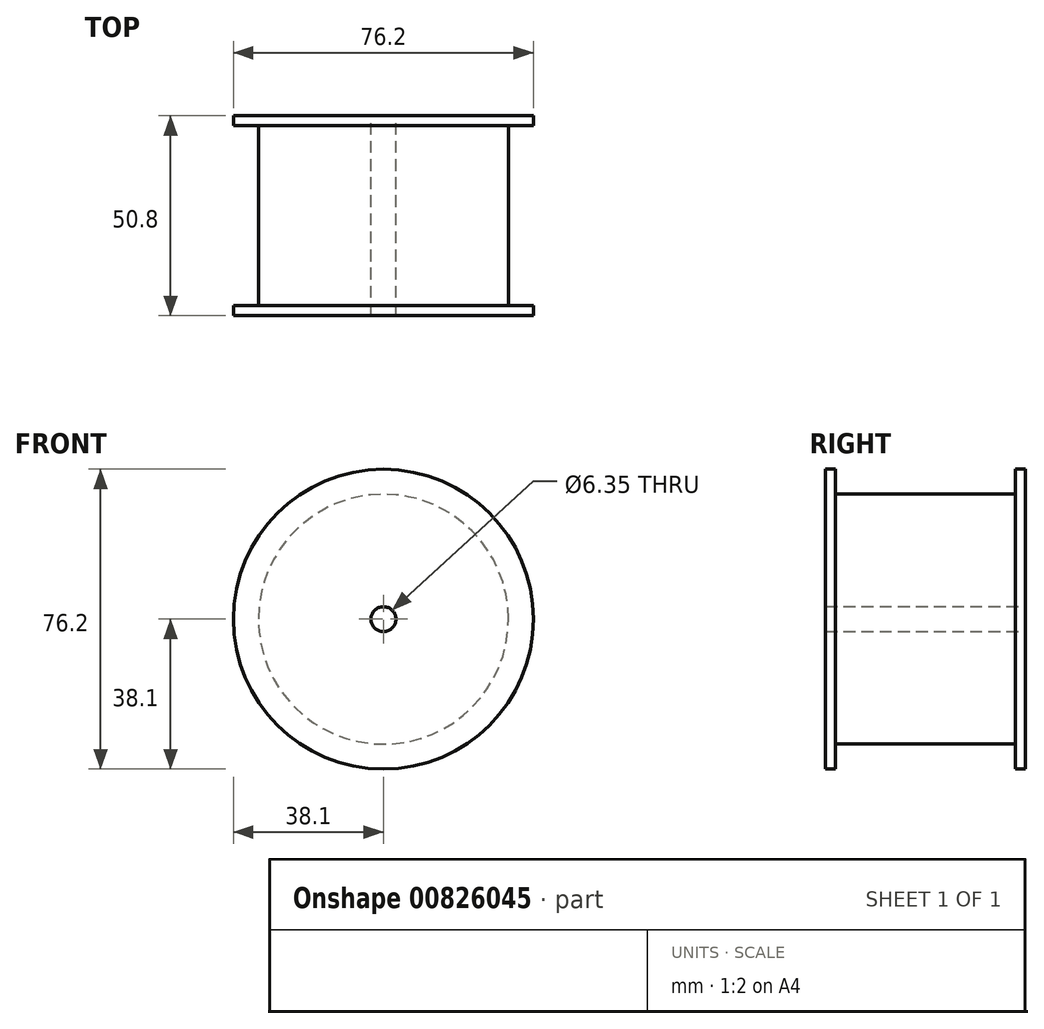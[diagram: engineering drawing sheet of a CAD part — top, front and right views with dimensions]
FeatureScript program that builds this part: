
annotation { "Feature Type Name" : "Feature", "Feature Type Description" : "" }
export const myFeature = defineFeature(function(context is Context, id is Id, definition is map)
    precondition{}
    {
        {
            var Q0;
            Q0=qCreatedBy(makeId("Front.planeOp"),FACE);
            var sketch = newSketch(context, id + "F0", { "sketchPlane" : qUnion([Q0])});
            skCircle(sketch, "E0", {"center": v(0, 0) * mm, "radius": 31.75 * mm});
            skCircle(sketch, "E1.0", {"center": v(0, 0) * mm, "radius": 38.1 * mm});
            skSolve(sketch);
        }
        {
            var Q0;
            Q0=makeQuery(id+"F0.imprint","IMPRINT",FACE,{"disambiguationData":[TD([[makeQuery(id+"F0.imprint","IMPRINT",EDGE,{"derivedFrom":sQuery(id+"F0.wireOp",EDGE,"E0")}),1.0]])]});
            var Q1;
            Q1=makeQuery(id+"F0.imprint","IMPRINT",FACE,{"disambiguationData":[TD([[makeQuery(id+"F0.imprint","IMPRINT",EDGE,{"derivedFrom":sQuery(id+"F0.wireOp",EDGE,"E0")}),-1.0]])]});
            extrude(context, id + "F1", {"entities" : qUnion([Q0, Q1]), "depth" : 25.4 * mm, "offsetDistance" : 25.4 * mm, "hasSecondDirection" : true, "secondDirectionOppositeDirection" : true, "secondDirectionDepth" : 25.4 * mm});
        }
        {
            var Q0;
            Q0=makeQuery(id+"F0.imprint","IMPRINT",FACE,{"disambiguationData":[TD([[makeQuery(id+"F0.imprint","IMPRINT",EDGE,{"derivedFrom":sQuery(id+"F0.wireOp",EDGE,"E0")}),-1.0]])]});
            extrude(context, id + "F2", {"entities" : qUnion([Q0]), "operationType" : NewBodyOperationType.REMOVE, "oppositeDirection" : true, "depth" : 22.86 * mm, "offsetDistance" : 25.4 * mm, "hasSecondDirection" : true, "secondDirectionOppositeDirection" : false, "secondDirectionDepth" : 22.86 * mm});
        }
        {
            var Q0;
            Q0=sQuery(id+"F0.wireOp",VERTEX,"E0.center");
            var Q1;
            Q1=makeQuery(id+"F1.opExtrude","SWEPT_BODY",BODY,{"disambiguationData":[OSD([sQuery(id+"F0.wireOp",EDGE,"E1.0")])]});
            hole(context, id + "F3", {"style" : HoleStyle.SIMPLE, "endStyle" : HoleEndStyle.THROUGH, "oppositeDirection" : true, "holeDiameter" : 6.35 * mm, "majorDiameter" : 6.35 * mm, "isTappedThrough" : true, "tappedDepth" : 12.7 * mm, "tapClearance" : 3, "locations" : qUnion([Q0]), "scope" : qUnion([Q1])});
        }
        {
            var Q0;
            Q0=sQuery(id+"F0.wireOp",VERTEX,"E0.center");
            var Q1;
            Q1=makeQuery(id+"F1.opExtrude","SWEPT_BODY",BODY,{"disambiguationData":[OSD([sQuery(id+"F0.wireOp",EDGE,"E1.0")])]});
            hole(context, id + "F4", {"style" : HoleStyle.SIMPLE, "endStyle" : HoleEndStyle.THROUGH, "holeDiameter" : 6.35 * mm, "majorDiameter" : 6.35 * mm, "isTappedThrough" : true, "tappedDepth" : 12.7 * mm, "tapClearance" : 3, "locations" : qUnion([Q0]), "scope" : qUnion([Q1])});
        }
    });
